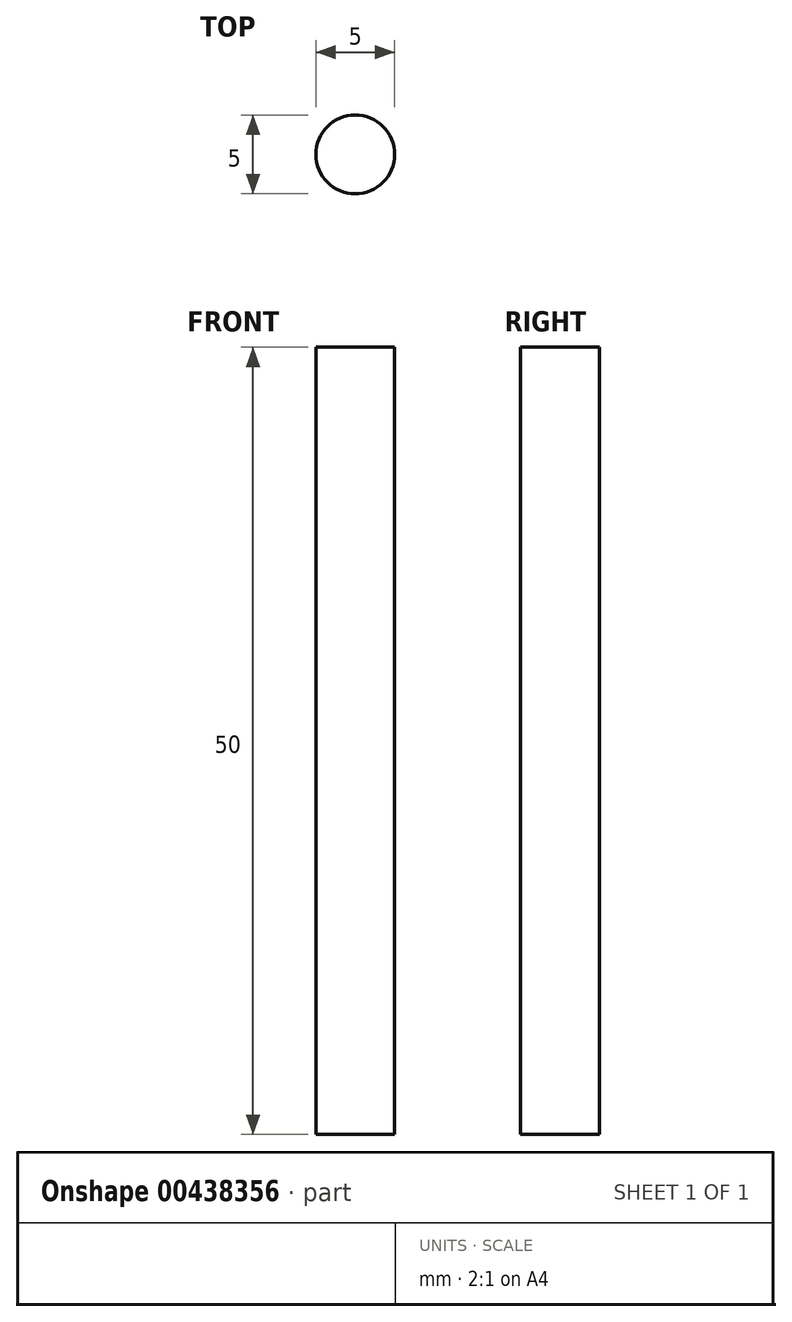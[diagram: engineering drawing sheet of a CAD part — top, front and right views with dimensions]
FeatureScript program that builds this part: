
annotation { "Feature Type Name" : "Feature", "Feature Type Description" : "" }
export const myFeature = defineFeature(function(context is Context, id is Id, definition is map)
    precondition{}
    {
        {
            var Q0;
            Q0=qCreatedBy(makeId("Top.planeOp"),FACE);
            var sketch = newSketch(context, id + "F0", { "sketchPlane" : qUnion([Q0])});
            skCircle(sketch, "E0", {"center": v(0, 0) * mm, "radius": 2.5 * mm});
            skSolve(sketch);
        }
        {
            var Q0;
            Q0=makeQuery(id+"F0.imprint","IMPRINT",FACE,{"disambiguationData":[TD([[makeQuery(id+"F0.imprint","IMPRINT",EDGE,{"derivedFrom":sQuery(id+"F0.wireOp",EDGE,"E0")}),1.0]])]});
            extrude(context, id + "F1", {"entities" : qUnion([Q0]), "depth" : 50 * mm});
        }
    });
